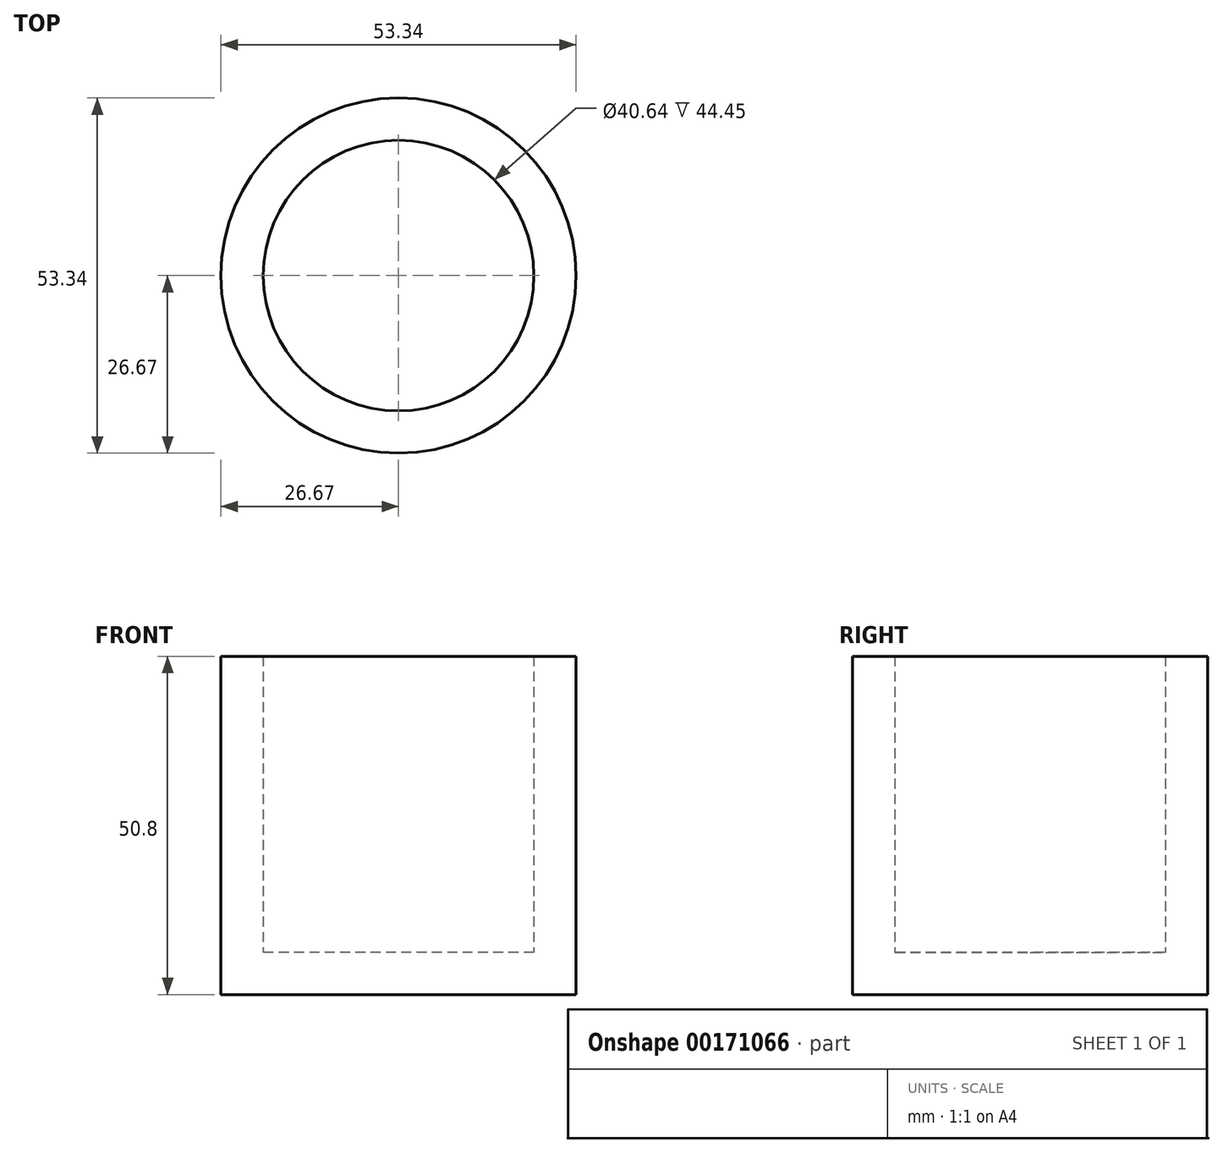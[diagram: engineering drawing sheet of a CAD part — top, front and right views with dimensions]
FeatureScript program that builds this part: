
annotation { "Feature Type Name" : "Feature", "Feature Type Description" : "" }
export const myFeature = defineFeature(function(context is Context, id is Id, definition is map)
    precondition{}
    {
        {
            var Q0;
            Q0=qCreatedBy(makeId("Top.planeOp"),FACE);
            var sketch = newSketch(context, id + "F0", { "sketchPlane" : qUnion([Q0])});
            skCircle(sketch, "E0", {"center": v(0, 0) * mm, "radius": 20.32 * mm});
            skCircle(sketch, "E1", {"center": v(0, 0) * mm, "radius": 26.67 * mm});
            skSolve(sketch);
        }
        {
            var Q0;
            Q0=makeQuery(id+"F0.imprint","IMPRINT",FACE,{"disambiguationData":[TD([[makeQuery(id+"F0.imprint","IMPRINT",EDGE,{"derivedFrom":sQuery(id+"F0.wireOp",EDGE,"E0")}),1.0]])]});
            var Q1;
            Q1=makeQuery(id+"F0.imprint","IMPRINT",FACE,{"disambiguationData":[TD([[makeQuery(id+"F0.imprint","IMPRINT",EDGE,{"derivedFrom":sQuery(id+"F0.wireOp",EDGE,"E0")}),-1.0]])]});
            extrude(context, id + "F1", {"entities" : qUnion([Q0, Q1]), "depth" : 50.8 * mm});
        }
        {
            var Q0;
            Q0=makeQuery(id+"F1.opExtrude","CAP_FACE",FACE,{"disambiguationData":[OSD([sQuery(id+"F0.wireOp",EDGE,"E1")])],"isStart":false});
            shell(context, id + "F2", {"entities" : qUnion([Q0]), "thickness" : 6.35 * mm});
        }
    });
